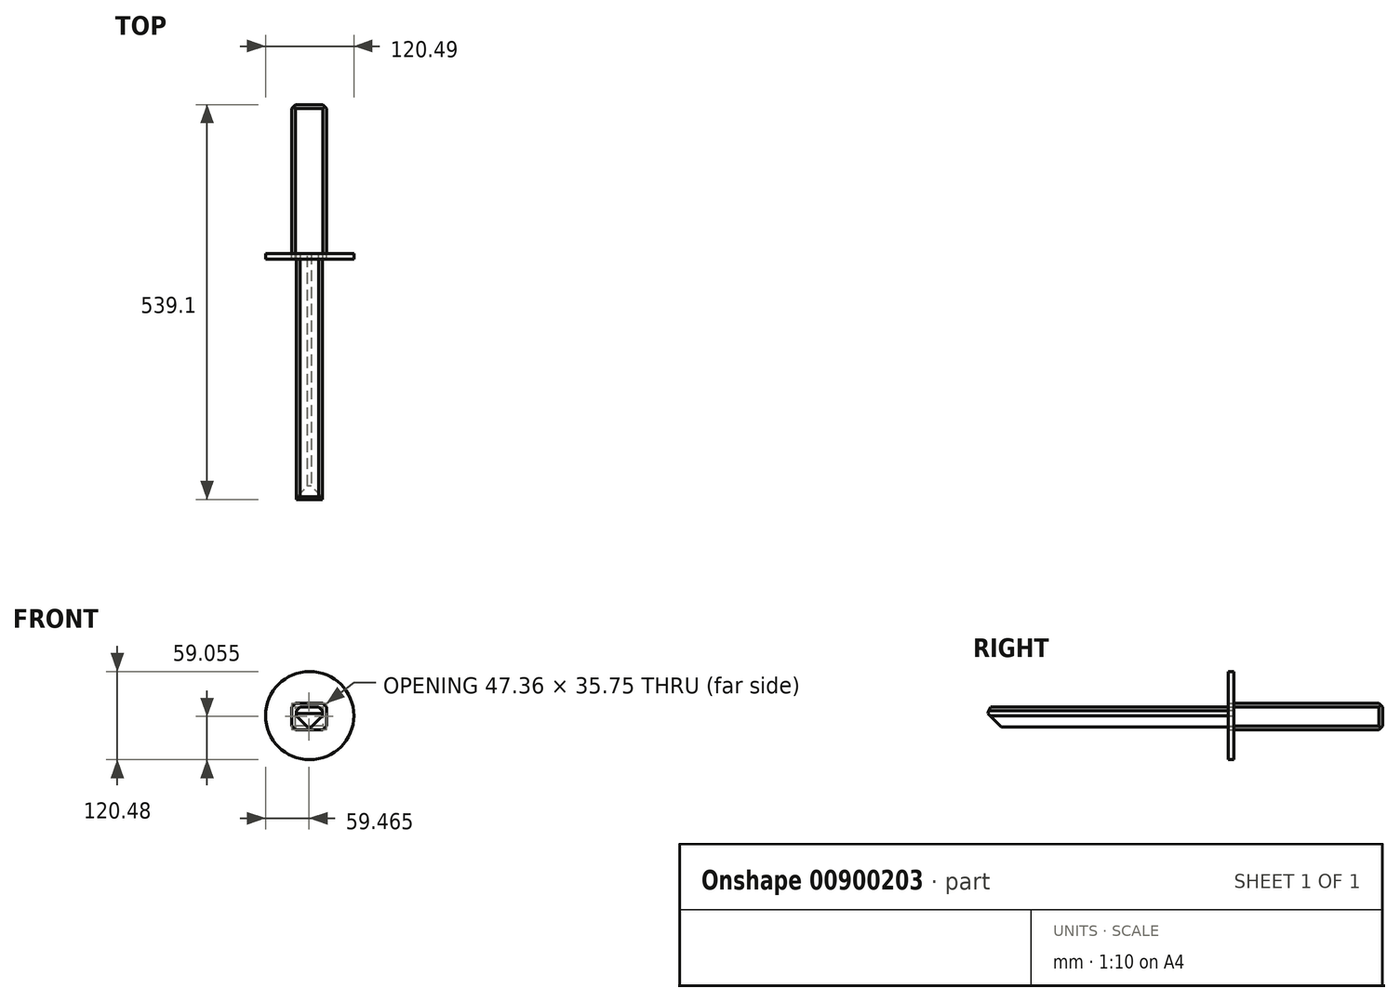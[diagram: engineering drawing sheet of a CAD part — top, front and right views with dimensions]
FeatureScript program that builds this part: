
annotation { "Feature Type Name" : "Feature", "Feature Type Description" : "" }
export const myFeature = defineFeature(function(context is Context, id is Id, definition is map)
    precondition{}
    {
        {
            var Q0;
            Q0=qCreatedBy(makeId("Front.planeOp"),FACE);
            var sketch = newSketch(context, id + "F0", { "sketchPlane" : qUnion([Q0])});
            skLineSegment(sketch, "E0.bottom", {"start": v(-54.83, 12.23) * mm, "end": v(-7.46, 12.23) * mm});
            skLineSegment(sketch, "E0.top", {"start": v(-54.83, -23.52) * mm, "end": v(-7.46, -23.52) * mm});
            skLineSegment(sketch, "E0.left", {"start": v(-54.83, 12.23) * mm, "end": v(-54.83, -23.52) * mm});
            skLineSegment(sketch, "E0.right", {"start": v(-7.46, 12.23) * mm, "end": v(-7.46, -23.52) * mm});
            skPoint(sketch, "E0.middle", {"position": v(-31.14, -5.64) * mm});
            skSolve(sketch);
        }
        {
            var Q0;
            Q0=makeQuery(id+"F0.imprint","IMPRINT",FACE,{"disambiguationData":[TD([[makeQuery(id+"F0.imprint","IMPRINT",EDGE,{"derivedFrom":sQuery(id+"F0.wireOp",EDGE,"E0.bottom")}),-1.0]])]});
            extrude(context, id + "F1", {"entities" : qUnion([Q0]), "depth" : -203.2 * mm, "offsetDistance" : 25.4 * mm});
        }
        {
            var Q0;
            Q0=makeQuery(id+"F1.opExtrude","SWEPT_EDGE",EDGE,{"disambiguationData":[OSD([sQuery(id+"F0.wireOp",EDGE,"E0.bottom"),sQuery(id+"F0.wireOp",EDGE,"E0.right")])]});
            var Q1;
            Q1=makeQuery(id+"F1.opExtrude","SWEPT_EDGE",EDGE,{"disambiguationData":[OSD([sQuery(id+"F0.wireOp",EDGE,"E0.bottom"),sQuery(id+"F0.wireOp",EDGE,"E0.left")])]});
            var Q2;
            Q2=makeQuery(id+"F1.opExtrude","SWEPT_EDGE",EDGE,{"disambiguationData":[OSD([sQuery(id+"F0.wireOp",EDGE,"E0.top"),sQuery(id+"F0.wireOp",EDGE,"E0.right")])]});
            chamfer(context, id + "F2", {"entities" : qUnion([Q0, Q1, Q2]), "width" : 5.08 * mm, "tangentPropagation" : true});
        }
        {
            var Q0;
            Q0=makeQuery(id+"F1.opExtrude","SWEPT_EDGE",EDGE,{"disambiguationData":[OSD([sQuery(id+"F0.wireOp",EDGE,"E0.top"),sQuery(id+"F0.wireOp",EDGE,"E0.left")])]});
            var Q1;
            Q1=makeQuery(id+"F1.opExtrude","CAP_EDGE",EDGE,{"disambiguationData":[OSD([sQuery(id+"F0.wireOp",EDGE,"E0.top")])],"isStart":false});
            var Q2;
            Q2=makeQuery(id+"F1.opExtrude","CAP_EDGE",EDGE,{"disambiguationData":[OSD([sQuery(id+"F0.wireOp",EDGE,"E0.left")])],"isStart":false});
            var Q3;
            Q3=makeQuery(id+"F1.opExtrude","CAP_EDGE",EDGE,{"disambiguationData":[OSD([sQuery(id+"F0.wireOp",EDGE,"E0.bottom")])],"isStart":false});
            var Q4;
            Q4=makeQuery(id+"F1.opExtrude","CAP_EDGE",EDGE,{"disambiguationData":[OSD([sQuery(id+"F0.wireOp",EDGE,"E0.right")])],"isStart":false});
            chamfer(context, id + "F3", {"entities" : qUnion([Q0, Q1, Q2, Q3, Q4]), "width" : 5.08 * mm, "tangentPropagation" : true});
        }
        {
            var Q0;
            Q0=makeQuery(id+"F1.opExtrude","CAP_FACE",FACE,{"disambiguationData":[OSD([sQuery(id+"F0.wireOp",EDGE,"E0.bottom"),sQuery(id+"F0.wireOp",EDGE,"E0.top"),sQuery(id+"F0.wireOp",EDGE,"E0.left"),sQuery(id+"F0.wireOp",EDGE,"E0.right")])],"isStart":true});
            var sketch = newSketch(context, id + "F4", { "sketchPlane" : qUnion([Q0])});
            skCircle(sketch, "E1", {"center": v(-30.36, -4.46) * mm, "radius": 60.24 * mm});
            skSolve(sketch);
        }
        {
            var Q0;
            Q0=makeQuery(id+"F4.imprint","IMPRINT",FACE,{"disambiguationData":[TD([[makeQuery(id+"F4.imprint","IMPRINT",EDGE,{"derivedFrom":sQuery(id+"F4.wireOp",EDGE,"E1")}),1.0]])]});
            extrude(context, id + "F5", {"entities" : qUnion([Q0]), "depth" : 7.62 * mm, "offsetDistance" : 25.4 * mm});
        }
        {
            var Q0;
            Q0=makeQuery(id+"F1.opExtrude","CAP_FACE",FACE,{"disambiguationData":[OSD([sQuery(id+"F0.wireOp",EDGE,"E0.bottom"),sQuery(id+"F0.wireOp",EDGE,"E0.top"),sQuery(id+"F0.wireOp",EDGE,"E0.left"),sQuery(id+"F0.wireOp",EDGE,"E0.right")])],"isStart":true});
            var sketch = newSketch(context, id + "F6", { "sketchPlane" : qUnion([Q0])});
            skLineSegment(sketch, "E2.bottom", {"start": v(-13, 7) * mm, "end": v(-48.44, 7) * mm});
            skLineSegment(sketch, "E2.top", {"start": v(-13, -20.07) * mm, "end": v(-48.44, -20.07) * mm});
            skLineSegment(sketch, "E2.left", {"start": v(-13, 7) * mm, "end": v(-13, -20.07) * mm});
            skLineSegment(sketch, "E2.right", {"start": v(-48.44, 7) * mm, "end": v(-48.44, -20.07) * mm});
            skPoint(sketch, "E2.middle", {"position": v(-30.72, -6.53) * mm});
            skSolve(sketch);
        }
        {
            var Q0;
            Q0=makeQuery(id+"F6.imprint","IMPRINT",FACE,{"disambiguationData":[TD([[makeQuery(id+"F6.imprint","IMPRINT",EDGE,{"derivedFrom":sQuery(id+"F6.wireOp",EDGE,"E2.bottom")}),1.0]])]});
            extrude(context, id + "F7", {"entities" : qUnion([Q0]), "operationType" : NewBodyOperationType.ADD, "depth" : 355.6 * mm, "offsetDistance" : 25.4 * mm});
        }
        {
            var Q0;
            Q0=makeQuery(id+"F7.opExtrude","SWEPT_EDGE",EDGE,{"disambiguationData":[OSD([sQuery(id+"F6.wireOp",EDGE,"E2.top"),sQuery(id+"F6.wireOp",EDGE,"E2.right")])]});
            var Q1;
            Q1=makeQuery(id+"F7.opExtrude","SWEPT_EDGE",EDGE,{"disambiguationData":[OSD([sQuery(id+"F6.wireOp",EDGE,"E2.top"),sQuery(id+"F6.wireOp",EDGE,"E2.left")])]});
            chamfer(context, id + "F8", {"entities" : qUnion([Q0, Q1]), "width" : 15.24 * mm, "tangentPropagation" : true});
        }
        {
            var Q0;
            Q0=makeQuery(id+"F7.opExtrude","CAP_EDGE",EDGE,{"disambiguationData":[OSD([sQuery(id+"F6.wireOp",EDGE,"E2.top")])],"isStart":false});
            chamfer(context, id + "F9", {"entities" : qUnion([Q0]), "width" : 38.1 * mm, "tangentPropagation" : true});
        }
        {
            var Q0;
            Q0=makeQuery(id+"F7.opExtrude","SWEPT_EDGE",EDGE,{"disambiguationData":[OSD([sQuery(id+"F6.wireOp",EDGE,"E2.bottom"),sQuery(id+"F6.wireOp",EDGE,"E2.right")])]});
            var Q1;
            Q1=makeQuery(id+"F9.opChamfer","BLEND_EDGE",EDGE,{"blendedFrom":[makeQuery(id+"F7.opExtrude","CAP_EDGE",EDGE,{"disambiguationData":[OSD([sQuery(id+"F6.wireOp",EDGE,"E2.top")])],"isStart":false}),makeQuery(id+"F7.opExtrude","SWEPT_FACE",FACE,{"disambiguationData":[OSD([sQuery(id+"F6.wireOp",EDGE,"E2.bottom")])]})],"blendedInto":[makeQuery(id+"F7.opExtrude","SWEPT_FACE",FACE,{"disambiguationData":[OSD([sQuery(id+"F6.wireOp",EDGE,"E2.bottom")])]})]});
            var Q2;
            Q2=makeQuery(id+"F7.opExtrude","SWEPT_EDGE",EDGE,{"disambiguationData":[OSD([sQuery(id+"F6.wireOp",EDGE,"E2.bottom"),sQuery(id+"F6.wireOp",EDGE,"E2.left")])]});
            chamfer(context, id + "F10", {"entities" : qUnion([Q0, Q1, Q2]), "width" : 5.08 * mm, "tangentPropagation" : true});
        }
    });
